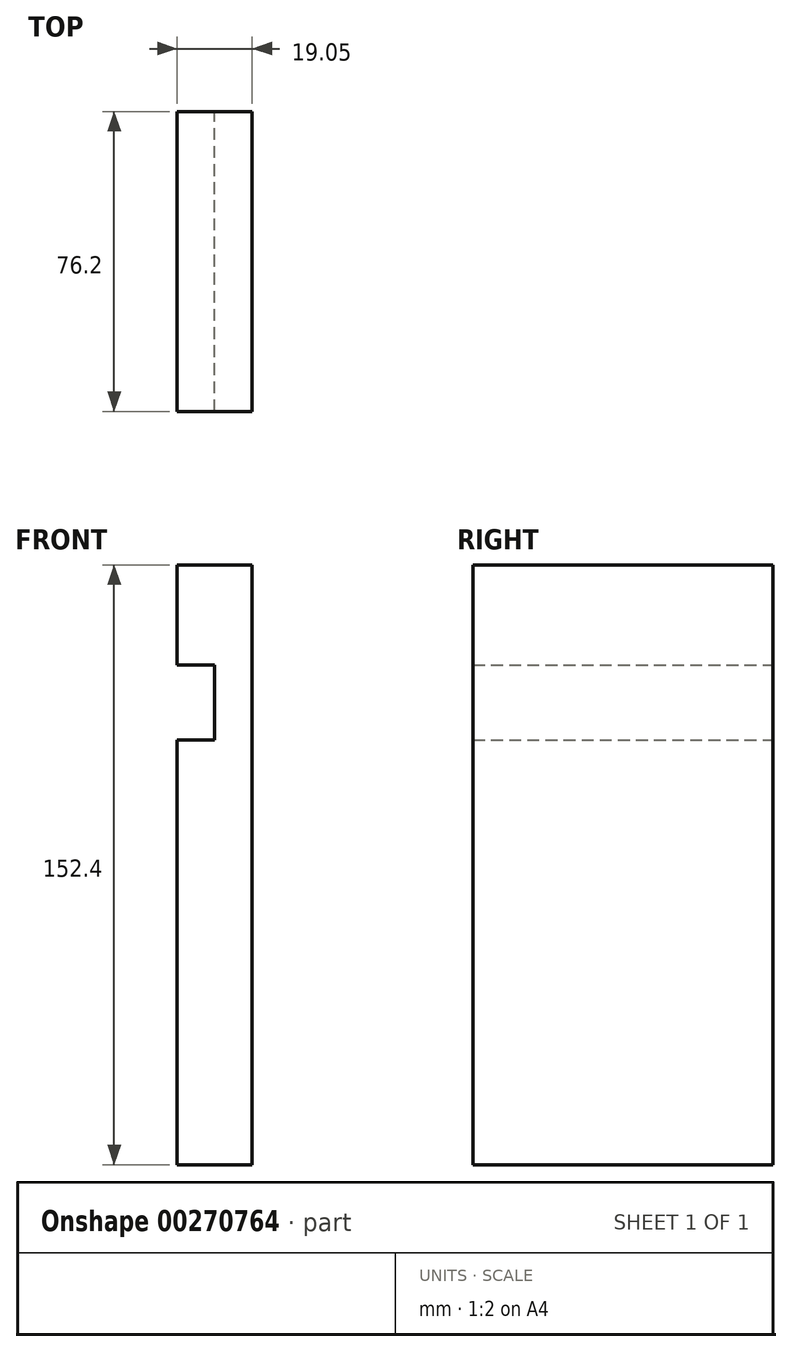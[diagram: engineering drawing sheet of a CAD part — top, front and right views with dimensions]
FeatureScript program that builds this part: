
annotation { "Feature Type Name" : "Feature", "Feature Type Description" : "" }
export const myFeature = defineFeature(function(context is Context, id is Id, definition is map)
    precondition{}
    {
        {
            var Q0;
            Q0=qCreatedBy(makeId("Front.planeOp"),FACE);
            var sketch = newSketch(context, id + "F0", { "sketchPlane" : qUnion([Q0])});
            skLineSegment(sketch, "E0", {"start": v(0, 78.83) * mm, "end": v(-19.05, 78.83) * mm});
            skLineSegment(sketch, "E1", {"start": v(-19.05, 78.83) * mm, "end": v(-19.05, 53.43) * mm});
            skLineSegment(sketch, "E2", {"start": v(-19.05, 53.43) * mm, "end": v(-9.52, 53.43) * mm});
            skLineSegment(sketch, "E3", {"start": v(-9.52, 53.43) * mm, "end": v(-9.52, 34.38) * mm});
            skLineSegment(sketch, "E4", {"start": v(-9.52, 34.38) * mm, "end": v(-19.05, 34.38) * mm});
            skLineSegment(sketch, "E5", {"start": v(-19.05, 34.38) * mm, "end": v(-19.05, -73.57) * mm});
            skLineSegment(sketch, "E6", {"start": v(-19.05, -73.57) * mm, "end": v(0, -73.57) * mm});
            skLineSegment(sketch, "E7", {"start": v(0, -73.57) * mm, "end": v(0, 78.83) * mm});
            skSolve(sketch);
        }
        {
            var Q0;
            Q0=makeQuery(id+"F0.imprint","IMPRINT",FACE,{"disambiguationData":[TD([[makeQuery(id+"F0.imprint","IMPRINT",EDGE,{"derivedFrom":sQuery(id+"F0.wireOp",EDGE,"E0")}),1.0]])]});
            extrude(context, id + "F1", {"entities" : qUnion([Q0]), "depth" : 76.2 * mm});
        }
    });
